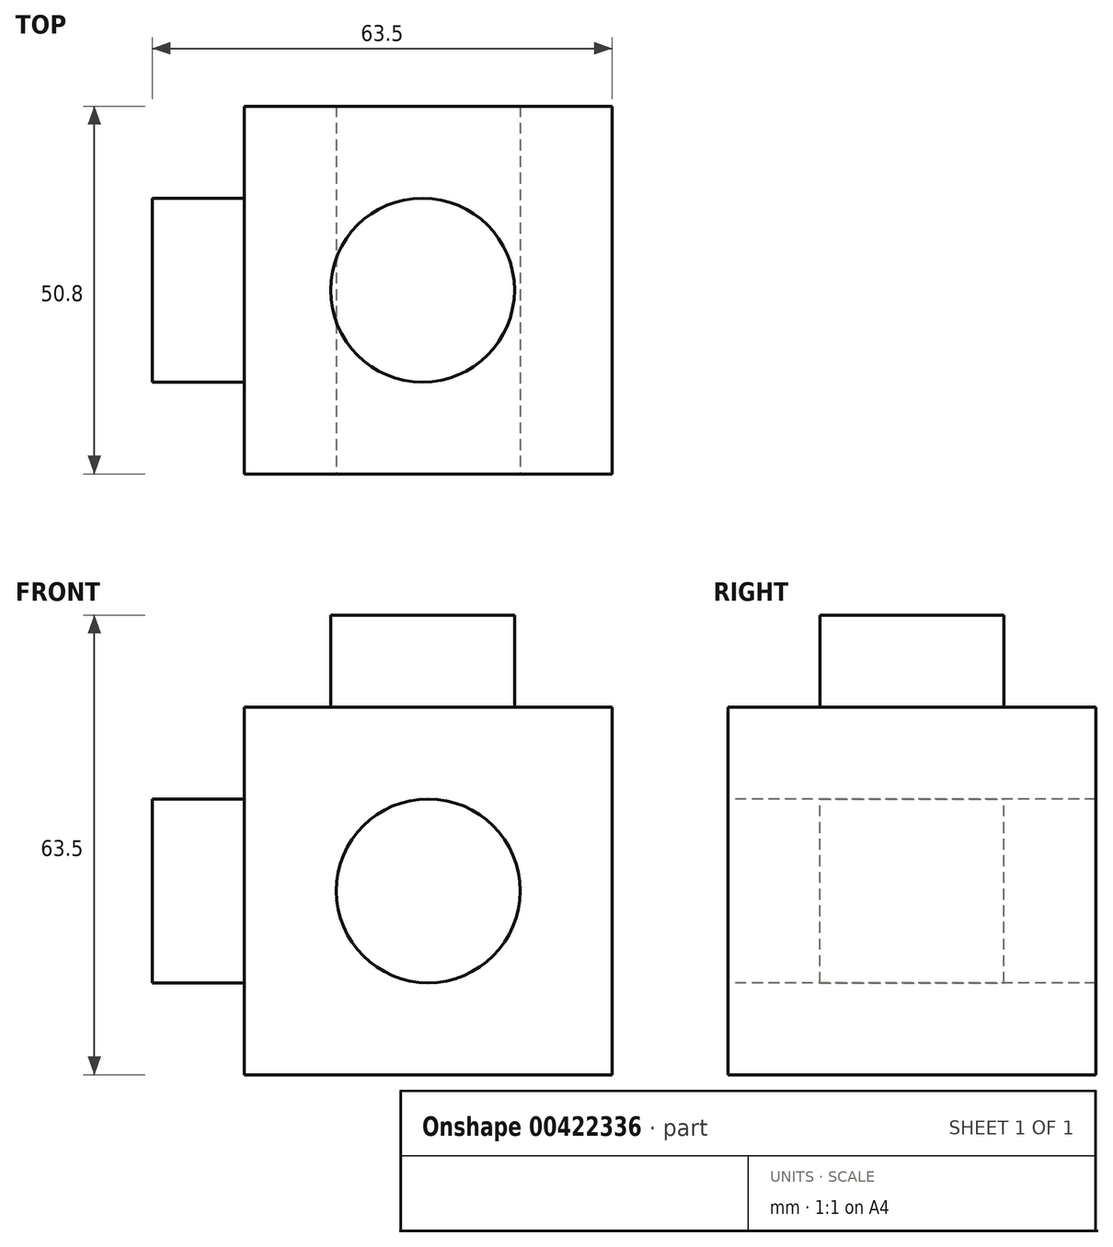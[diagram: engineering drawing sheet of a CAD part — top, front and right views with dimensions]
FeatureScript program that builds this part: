
annotation { "Feature Type Name" : "Feature", "Feature Type Description" : "" }
export const myFeature = defineFeature(function(context is Context, id is Id, definition is map)
    precondition{}
    {
        {
            var Q0;
            Q0=qCreatedBy(makeId("Front.planeOp"),FACE);
            var sketch = newSketch(context, id + "F0", { "sketchPlane" : qUnion([Q0])});
            skLineSegment(sketch, "E0.bottom", {"start": v(0, 0) * mm, "end": v(-50.8, 0) * mm});
            skLineSegment(sketch, "E0.top", {"start": v(0, 50.8) * mm, "end": v(-50.8, 50.8) * mm});
            skLineSegment(sketch, "E0.left", {"start": v(0, 0) * mm, "end": v(0, 50.8) * mm});
            skLineSegment(sketch, "E0.right", {"start": v(-50.8, 0) * mm, "end": v(-50.8, 50.8) * mm});
            skSolve(sketch);
        }
        {
            var Q0;
            Q0 = qSketchRegion(id + "F0", true);
            extrude(context, id + "F1", {"entities" : qUnion([Q0]), "depth" : 50.8 * mm});
        }
        {
            var Q0;
            Q0=makeQuery(id+"F1.opExtrude","CAP_FACE",FACE,{"disambiguationData":[OSD([sQuery(id+"F0.wireOp",EDGE,"E0.bottom"),sQuery(id+"F0.wireOp",EDGE,"E0.top"),sQuery(id+"F0.wireOp",EDGE,"E0.left"),sQuery(id+"F0.wireOp",EDGE,"E0.right")])],"isStart":false});
            var sketch = newSketch(context, id + "F2", { "sketchPlane" : qUnion([Q0])});
            skCircle(sketch, "E1", {"center": v(-25.4, 25.4) * mm, "radius": 12.7 * mm});
            skSolve(sketch);
        }
        {
            var Q0;
            Q0 = qSketchRegion(id + "F2", true);
            extrude(context, id + "F3", {"entities" : qUnion([Q0]), "operationType" : NewBodyOperationType.REMOVE, "oppositeDirection" : true, "depth" : 50.8 * mm});
        }
        {
            var Q0;
            Q0=makeQuery(id+"F1.opExtrude","SWEPT_FACE",FACE,{"disambiguationData":[OSD([sQuery(id+"F0.wireOp",EDGE,"E0.right")])]});
            var sketch = newSketch(context, id + "F4", { "sketchPlane" : qUnion([Q0])});
            skLineSegment(sketch, "E2.bottom", {"start": v(38.1, 12.7) * mm, "end": v(12.7, 12.7) * mm});
            skLineSegment(sketch, "E2.top", {"start": v(38.1, 38.1) * mm, "end": v(12.7, 38.1) * mm});
            skLineSegment(sketch, "E2.left", {"start": v(38.1, 12.7) * mm, "end": v(38.1, 38.1) * mm});
            skLineSegment(sketch, "E2.right", {"start": v(12.7, 12.7) * mm, "end": v(12.7, 38.1) * mm});
            skSolve(sketch);
        }
        {
            var Q0;
            Q0 = qSketchRegion(id + "F4", true);
            extrude(context, id + "F5", {"entities" : qUnion([Q0]), "operationType" : NewBodyOperationType.ADD, "depth" : 12.7 * mm});
        }
        {
            var Q0;
            Q0=makeQuery(id+"F1.opExtrude","SWEPT_FACE",FACE,{"disambiguationData":[OSD([sQuery(id+"F0.wireOp",EDGE,"E0.top")])]});
            var sketch = newSketch(context, id + "F6", { "sketchPlane" : qUnion([Q0])});
            skCircle(sketch, "E3", {"center": v(-26.2, -25.41) * mm, "radius": 12.7 * mm});
            skSolve(sketch);
        }
        {
            var Q0;
            Q0 = qSketchRegion(id + "F6", true);
            extrude(context, id + "F7", {"entities" : qUnion([Q0]), "operationType" : NewBodyOperationType.ADD, "depth" : 12.7 * mm});
        }
    });
